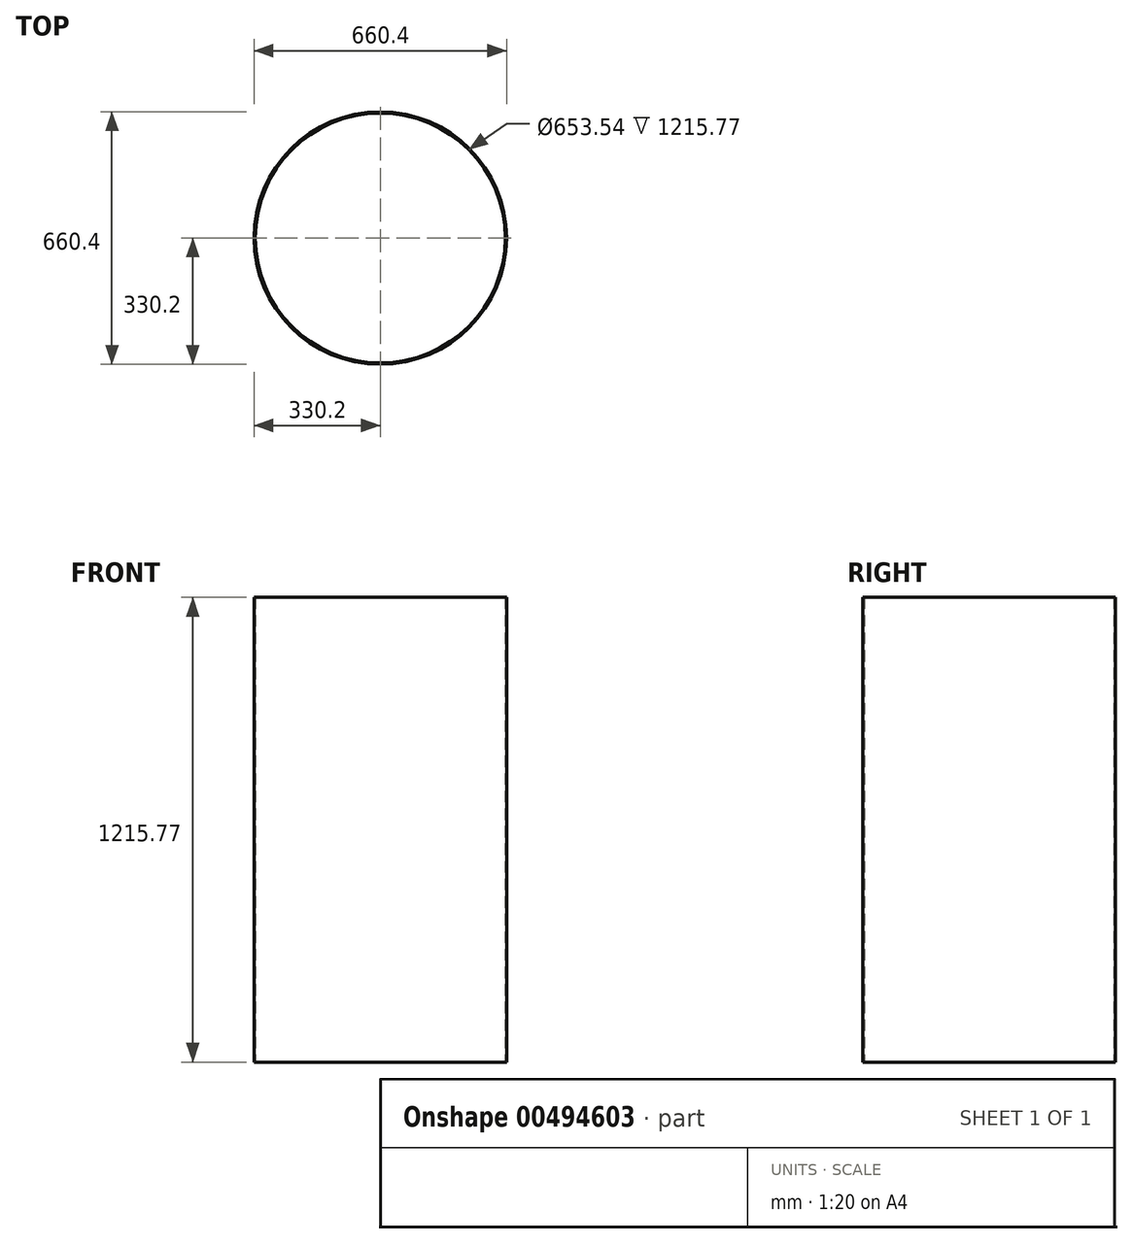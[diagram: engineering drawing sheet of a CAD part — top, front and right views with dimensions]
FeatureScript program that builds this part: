
annotation { "Feature Type Name" : "Feature", "Feature Type Description" : "" }
export const myFeature = defineFeature(function(context is Context, id is Id, definition is map)
    precondition{}
    {
        {
            var Q0;
            Q0=qCreatedBy(makeId("Top.planeOp"),FACE);
            var sketch = newSketch(context, id + "F0", { "sketchPlane" : qUnion([Q0])});
            skCircle(sketch, "E0", {"center": v(0, 0) * mm, "radius": 330.2 * mm});
            skCircle(sketch, "E1.0", {"center": v(0, 0) * mm, "radius": 326.77 * mm});
            skSolve(sketch);
        }
        {
            var Q0;
            Q0 = qSketchRegion(id + "F0", true);
            extrude(context, id + "F1", {"entities" : qUnion([Q0]), "depth" : 1215.77 * mm, "offsetDistance" : 25.4 * mm});
        }
    });
